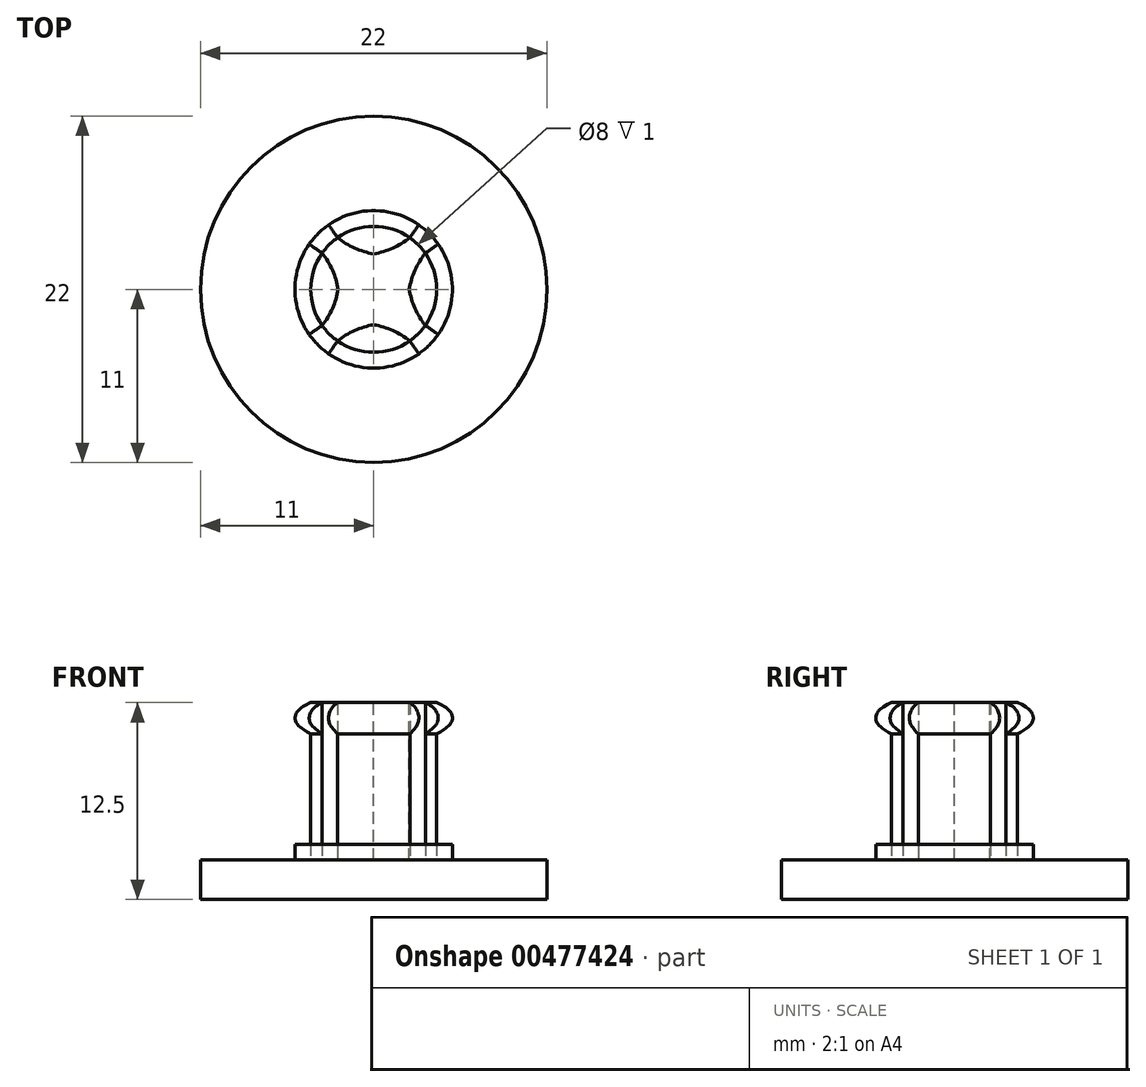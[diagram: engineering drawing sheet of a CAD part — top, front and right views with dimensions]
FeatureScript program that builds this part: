
annotation { "Feature Type Name" : "Feature", "Feature Type Description" : "" }
export const myFeature = defineFeature(function(context is Context, id is Id, definition is map)
    precondition{}
    {
        {
            var Q0;
            Q0=qCreatedBy(makeId("Top.planeOp"),FACE);
            var sketch = newSketch(context, id + "F0", { "sketchPlane" : qUnion([Q0])});
            skCircle(sketch, "E0", {"center": v(0, 0) * mm, "radius": 11 * mm});
            skCircle(sketch, "E1", {"center": v(0, 0) * mm, "radius": 4 * mm});
            skCircle(sketch, "E2.0", {"center": v(0, 0) * mm, "radius": 3.8 * mm});
            skSolve(sketch);
        }
        {
            var Q0;
            Q0=makeQuery(id+"F0.imprint","IMPRINT",FACE,{"disambiguationData":[TD([[makeQuery(id+"F0.imprint","IMPRINT",EDGE,{"derivedFrom":sQuery(id+"F0.wireOp",EDGE,"E1")}),1.0]])]});
            var Q1;
            Q1=makeQuery(id+"F0.imprint","IMPRINT",FACE,{"disambiguationData":[TD([[makeQuery(id+"F0.imprint","IMPRINT",EDGE,{"derivedFrom":sQuery(id+"F0.wireOp",EDGE,"E0")}),1.0]])]});
            var Q2;
            Q2=makeQuery(id+"F0.imprint","IMPRINT",FACE,{"disambiguationData":[TD([[makeQuery(id+"F0.imprint","IMPRINT",EDGE,{"derivedFrom":sQuery(id+"F0.wireOp",EDGE,"E2.0")}),1.0]])]});
            extrude(context, id + "F1", {"entities" : qUnion([Q0, Q1, Q2]), "depth" : 2.5 * mm});
        }
        {
            var Q0;
            Q0=qCreatedBy(makeId("Right.planeOp"),FACE);
            var sketch = newSketch(context, id + "F2", { "sketchPlane" : qUnion([Q0])});
            skLineSegment(sketch, "E3", {"start": v(2.23, 2.5) * mm, "end": v(2.23, 12.5) * mm});
            skLineSegment(sketch, "E4", {"start": v(4, 12.5) * mm, "end": v(4, 0) * mm});
            skLineSegment(sketch, "E5", {"start": v(2.23, 12.5) * mm, "end": v(4, 12.5) * mm});
            skFitSpline(sketch, "E6", {"points": [v(4, 12.5) * mm, v(5, 11.5) * mm, v(4, 10.5) * mm], "startDerivative": vector(4.82, -1.91) * mm, "endDerivative": vector(-4.73, -2.8) * mm});
            skLineSegment(sketch, "E7", {"start": v(2.23, 2.5) * mm, "end": v(4, 2.5) * mm});
            skLineSegment(sketch, "E8", {"start": v(0, 0) * mm, "end": v(0, 11.97) * mm});
            skSolve(sketch);
        }
        {
            var Q0;
            Q0=makeQuery(id+"F2.imprint","IMPRINT",FACE,{"disambiguationData":[TD([[makeQuery(id+"F2.imprint","IMPRINT",EDGE,{"derivedFrom":sQuery(id+"F2.wireOp",EDGE,"E3")}),-1.0]])]});
            var Q1;
            {var subQ0=sQuery(id+"F2.wireOp",EDGE,"E6");Q1=makeQuery(id+"F2.imprint","IMPRINT",FACE,{"disambiguationData":[TD([[makeQuery(id+"F2.imprint","IMPRINT",EDGE,{"derivedFrom":subQ0}),-1.0]])]});}
            var Q2;
            Q2=sQuery(id+"F2.wireOp",EDGE,"E8");
            revolve(context, id + "F3", {"entities" : qUnion([Q0, Q1]), "axis" : qUnion([Q2]), "revolveType" : RevolveType.SYMMETRIC, "angle" : 70 * degree});
        }
        {
            var Q0;
            Q0=makeQuery(id+"F3.opRevolve","CAP_EDGE",EDGE,{"disambiguationData":[OSD([sQuery(id+"F2.wireOp",EDGE,"E3")])],"isStart":false});
            var Q1;
            Q1=makeQuery(id+"F3.opRevolve","CAP_EDGE",EDGE,{"disambiguationData":[OSD([sQuery(id+"F2.wireOp",EDGE,"E3")])],"isStart":true});
            fillet(context, id + "F4", {"entities" : qUnion([Q0, Q1]), "radius" : 5 * mm, "tangentPropagation" : true, "allowEdgeOverflow" : false});
        }
        {
            var Q0;
            Q0=makeQuery(id+"F3.opRevolve","SWEPT_BODY",BODY,{"disambiguationData":[OSD([sQuery(id+"F2.wireOp",EDGE,"E3"),sQuery(id+"F2.wireOp",EDGE,"E4"),sQuery(id+"F2.wireOp",EDGE,"E5"),sQuery(id+"F2.wireOp",EDGE,"E6"),sQuery(id+"F2.wireOp",EDGE,"E7")])]});
            var Q1;
            Q1=sQuery(id+"F2.wireOp",EDGE,"E8");
            circularPattern(context, id + "F5", {"entities" : qUnion([Q0]), "axis" : qUnion([Q1]), "angle" : 360 * degree, "instanceCount" : 4, "equalSpace" : true});
        }
        {
            var Q0;
            Q0=makeQuery(id+"F1.opExtrude","SWEPT_BODY",BODY,{"disambiguationData":[OSD([sQuery(id+"F0.wireOp",EDGE,"E0")])]});
            transform(context, id + "F6", {"entities" : qUnion([Q0]), "transformType" : TransformType.TRANSLATION_3D, "dx" : 0 * mm, "dy" : 0 * mm, "dz" : 0 * mm, "makeCopy" : true});
        }
        {
            var Q0;
            Q0=makeQuery(id+"F1.opExtrude","CAP_FACE",FACE,{"disambiguationData":[OSD([sQuery(id+"F0.wireOp",EDGE,"E0")])],"isStart":false});
            var sketch = newSketch(context, id + "F7", { "sketchPlane" : qUnion([Q0])});
            skCircle(sketch, "E9", {"center": v(0, 0) * mm, "radius": 4 * mm});
            skCircle(sketch, "E10.0", {"center": v(0, 0) * mm, "radius": 5 * mm});
            skSolve(sketch);
        }
        {
            var Q0;
            Q0 = qSketchRegion(id + "F7", true);
            extrude(context, id + "F8", {"entities" : qUnion([Q0]), "depth" : 1 * mm});
        }
    });
